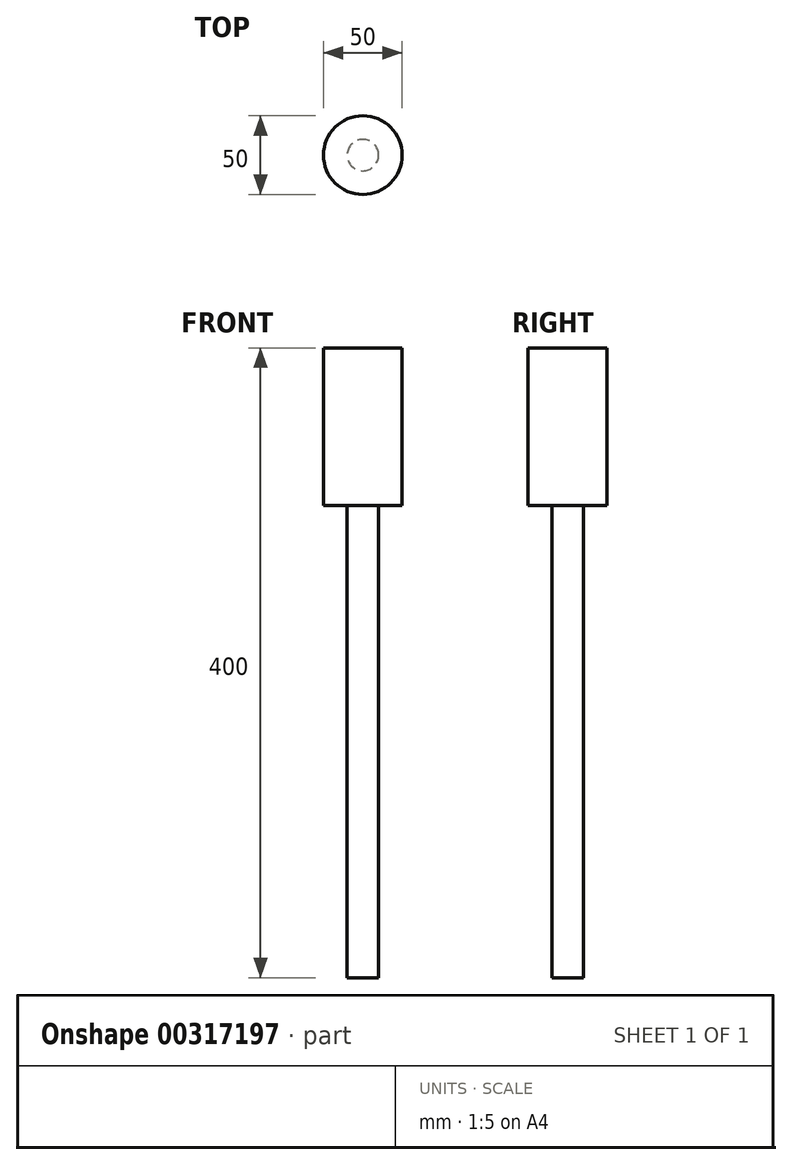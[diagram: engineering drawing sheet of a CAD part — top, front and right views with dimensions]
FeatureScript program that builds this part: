
annotation { "Feature Type Name" : "Feature", "Feature Type Description" : "" }
export const myFeature = defineFeature(function(context is Context, id is Id, definition is map)
    precondition{}
    {
        {
            var Q0;
            Q0=qCreatedBy(makeId("Top.planeOp"),FACE);
            var sketch = newSketch(context, id + "F0", { "sketchPlane" : qUnion([Q0])});
            skCircle(sketch, "E0", {"center": v(0, 0) * mm, "radius": 25 * mm});
            skSolve(sketch);
        }
        {
            var Q0;
            Q0 = qSketchRegion(id + "F0", true);
            extrude(context, id + "F1", {"entities" : qUnion([Q0]), "depth" : 100 * mm, "hasSecondDirection" : true, "secondDirectionOppositeDirection" : true, "secondDirectionDepth" : 300 * mm});
        }
        {
            var Q0;
            Q0=qCreatedBy(makeId("Top.planeOp"),FACE);
            var sketch = newSketch(context, id + "F2", { "sketchPlane" : qUnion([Q0])});
            skCircle(sketch, "E1", {"center": v(0, 0) * mm, "radius": 25 * mm});
            skCircle(sketch, "E2", {"center": v(0, 0) * mm, "radius": 10 * mm});
            skSolve(sketch);
        }
        {
            var Q0;
            Q0 = qSketchRegion(id + "F2", true);
            extrude(context, id + "F3", {"entities" : qUnion([Q0]), "operationType" : NewBodyOperationType.REMOVE, "oppositeDirection" : true, "depth" : 300 * mm});
        }
    });
